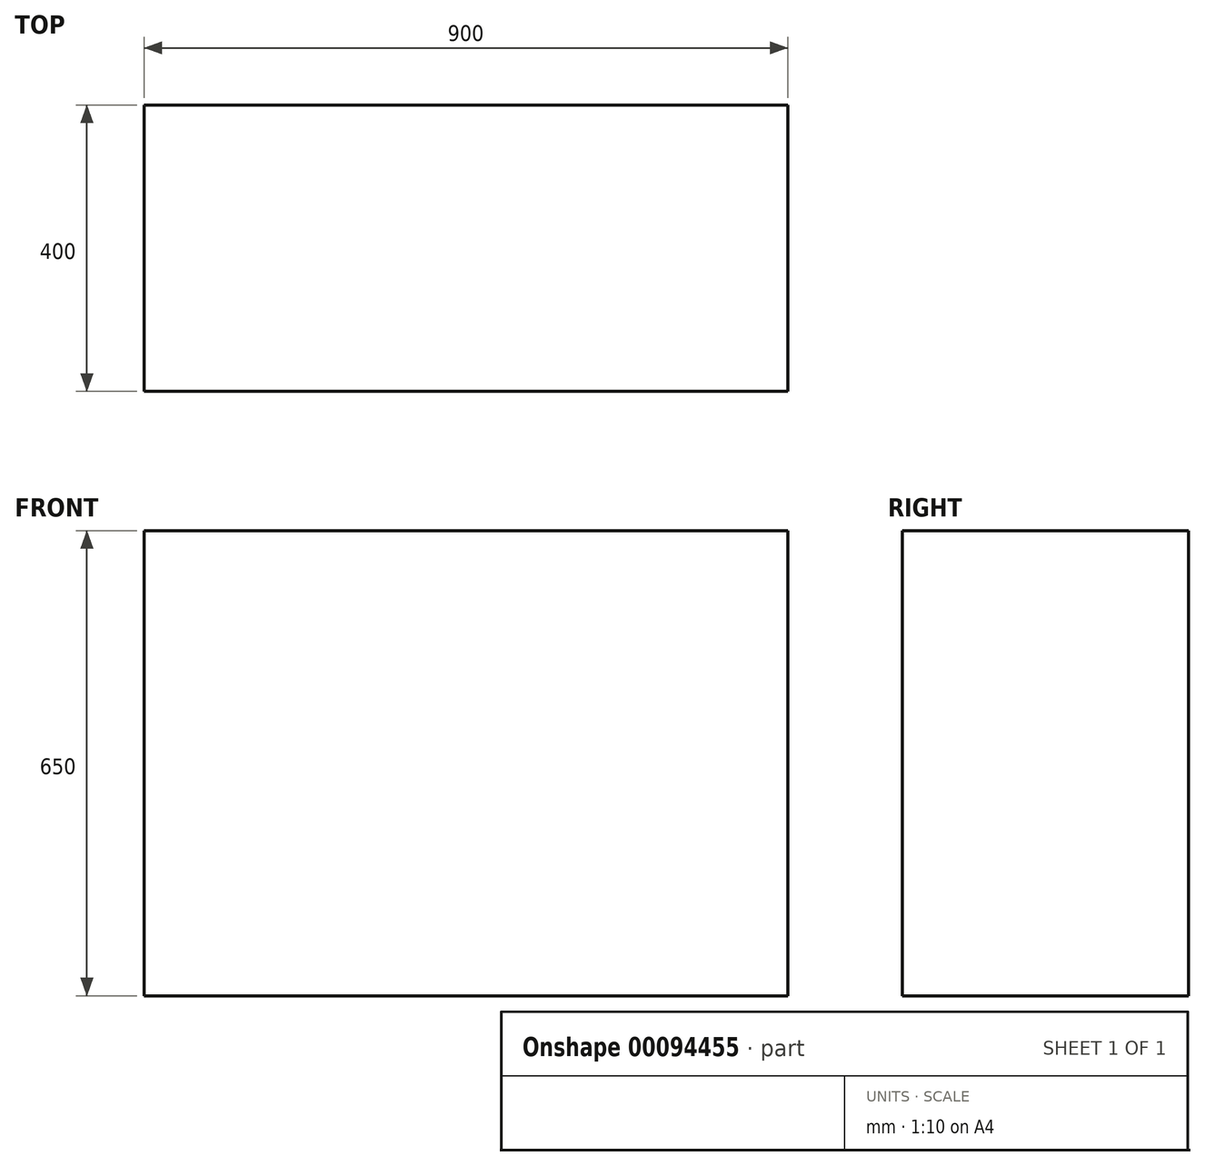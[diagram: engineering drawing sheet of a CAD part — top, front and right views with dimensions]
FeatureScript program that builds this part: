
annotation { "Feature Type Name" : "Feature", "Feature Type Description" : "" }
export const myFeature = defineFeature(function(context is Context, id is Id, definition is map)
    precondition{}
    {
        {
            var Q0;
            Q0=qCreatedBy(makeId("Front.planeOp"),FACE);
            var sketch = newSketch(context, id + "F0", { "sketchPlane" : qUnion([Q0])});
            skLineSegment(sketch, "E0.bottom", {"start": v(-450, 325) * mm, "end": v(450, 325) * mm});
            skLineSegment(sketch, "E0.top", {"start": v(-450, -325) * mm, "end": v(450, -325) * mm});
            skLineSegment(sketch, "E0.left", {"start": v(-450, 325) * mm, "end": v(-450, -325) * mm});
            skLineSegment(sketch, "E0.right", {"start": v(450, 325) * mm, "end": v(450, -325) * mm});
            skPoint(sketch, "E0.middle", {"position": v(0, 0) * mm});
            skSolve(sketch);
        }
        {
            var Q0;
            Q0 = qSketchRegion(id + "F0", true);
            extrude(context, id + "F1", {"entities" : qUnion([Q0]), "depth" : 400 * mm});
        }
    });
